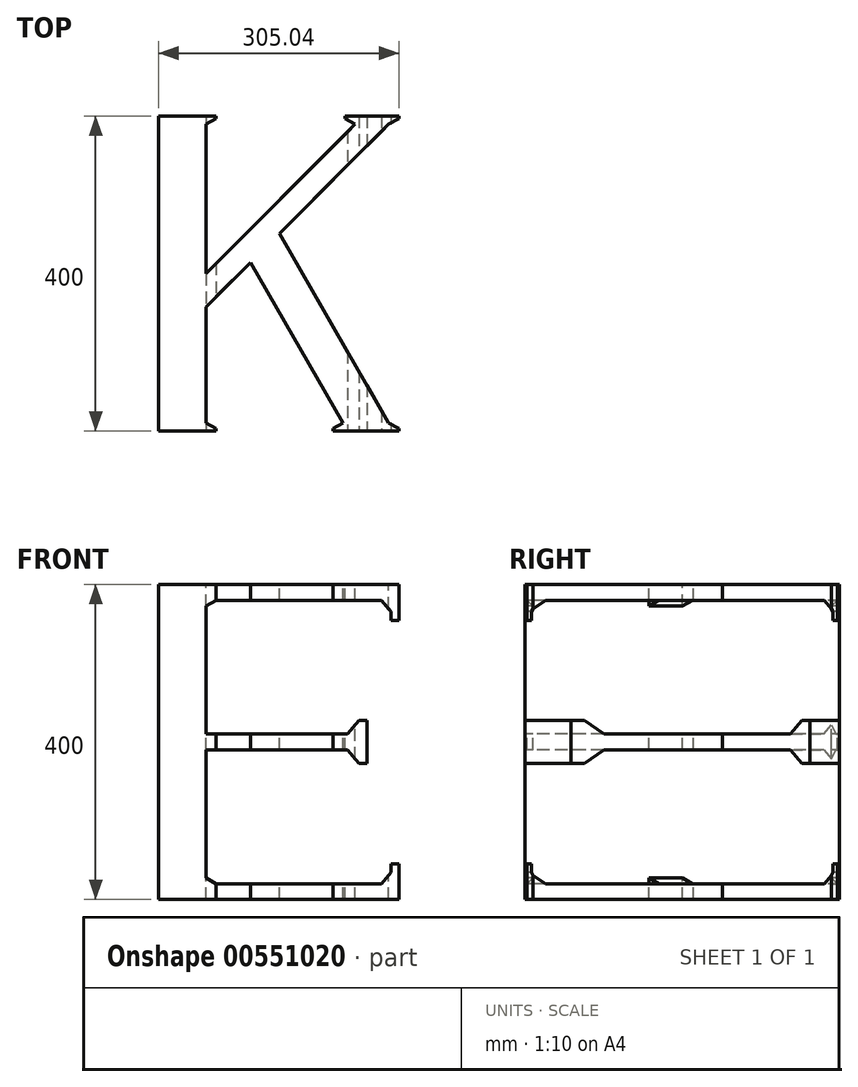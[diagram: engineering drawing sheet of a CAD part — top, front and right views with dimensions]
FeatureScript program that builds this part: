
annotation { "Feature Type Name" : "Feature", "Feature Type Description" : "" }
export const myFeature = defineFeature(function(context is Context, id is Id, definition is map)
    precondition{}
    {
        {
            var Q0;
            Q0=qCreatedBy(makeId("Front.planeOp"),FACE);
            var sketch = newSketch(context, id + "F0", { "sketchPlane" : qUnion([Q0])});
            skLineSegment(sketch, "E0.bottom", {"start": v(-197.15, 238.44) * mm, "end": v(107.89, 238.44) * mm});
            skLineSegment(sketch, "E0.top", {"start": v(-197.15, -161.56) * mm, "end": v(107.89, -161.56) * mm});
            skLineSegment(sketch, "E0.left", {"start": v(-197.15, 238.44) * mm, "end": v(-197.15, -161.56) * mm});
            skLineSegment(sketch, "E0.right", {"start": v(107.89, 238.44) * mm, "end": v(107.89, -161.56) * mm});
            skSolve(sketch);
        }
        {
            var Q0;
            Q0 = qSketchRegion(id + "F0", true);
            extrude(context, id + "F1", {"entities" : qUnion([Q0]), "depth" : 400 * mm, "offsetDistance" : 25.4 * mm});
        }
        {
            var Q0;
            Q0=makeQuery(id+"F1.opExtrude","SWEPT_FACE",FACE,{"disambiguationData":[OSD([sQuery(id+"F0.wireOp",EDGE,"E0.bottom")])]});
            var sketch = newSketch(context, id + "F2", { "sketchPlane" : qUnion([Q0])});
            skLineSegment(sketch, "E1", {"start": v(-197.15, -200) * mm, "end": v(0, -200) * mm, "construction": true});
            skLineSegment(sketch, "E2", {"start": v(-154.16, -400) * mm, "end": v(-154.16, -217.1) * mm, "construction": true});
            skLineSegment(sketch, "E3.MirrorCS", {"start": v(-137.15, -10.38) * mm, "end": v(-137.15, -200) * mm});
            skLineSegment(sketch, "E4.MirrorCS", {"start": v(-124.16, -2.88) * mm, "end": v(-137.15, -10.38) * mm});
            skLineSegment(sketch, "E5.MirrorCS", {"start": v(-124.16, -397.12) * mm, "end": v(-137.15, -389.62) * mm});
            skLineSegment(sketch, "E6", {"start": v(-124.16, -2.88) * mm, "end": v(-124.16, 0) * mm});
            skLineSegment(sketch, "E7", {"start": v(-124.16, -397.12) * mm, "end": v(-124.16, -400) * mm});
            skLineSegment(sketch, "E8", {"start": v(-137.15, -200) * mm, "end": v(52.47, -10.38) * mm});
            skLineSegment(sketch, "E9", {"start": v(-171.17, -10.38) * mm, "end": v(-197.15, -10.38) * mm, "construction": true});
            skLineSegment(sketch, "E10", {"start": v(52.47, -10.38) * mm, "end": v(39.48, -2.88) * mm});
            skLineSegment(sketch, "E11", {"start": v(39.48, -2.88) * mm, "end": v(39.48, 0) * mm});
            skLineSegment(sketch, "E12", {"start": v(-184.16, -10.38) * mm, "end": v(107.89, -10.38) * mm, "construction": true});
            skLineSegment(sketch, "E13", {"start": v(-137.15, -242.43) * mm, "end": v(-80.52, -185.8) * mm});
            skLineSegment(sketch, "E14", {"start": v(94.9, -10.38) * mm, "end": v(107.89, -2.88) * mm});
            skLineSegment(sketch, "E15", {"start": v(107.89, -2.88) * mm, "end": v(107.89, 0) * mm});
            skLineSegment(sketch, "E16", {"start": v(-80.52, -185.8) * mm, "end": v(37.16, -389.62) * mm});
            skLineSegment(sketch, "E17", {"start": v(-43.91, -149.2) * mm, "end": v(94.9, -389.62) * mm});
            skLineSegment(sketch, "E18", {"start": v(-171.17, -389.62) * mm, "end": v(107.89, -389.62) * mm, "construction": true});
            skLineSegment(sketch, "E19", {"start": v(94.9, -10.38) * mm, "end": v(94.9, -400) * mm, "construction": true});
            skPoint(sketch, "E20", {"position": v(94.9, -389.62) * mm});
            skLineSegment(sketch, "E21.MirrorCS", {"start": v(107.89, -397.12) * mm, "end": v(94.9, -389.62) * mm});
            skLineSegment(sketch, "E22.MirrorCS", {"start": v(37.16, -389.62) * mm, "end": v(24.17, -397.12) * mm});
            skLineSegment(sketch, "E23", {"start": v(24.17, -397.12) * mm, "end": v(24.17, -400) * mm});
            skLineSegment(sketch, "E24", {"start": v(107.89, -397.12) * mm, "end": v(107.89, -400) * mm});
            skPoint(sketch, "E25.orphan", {"position": v(39.33, -393.37) * mm});
            skPoint(sketch, "E26.orphan", {"position": v(97.06, -393.37) * mm});
            skLineSegment(sketch, "E27.trimOffspring", {"start": v(-43.91, -149.2) * mm, "end": v(94.9, -10.38) * mm});
            skLineSegment(sketch, "E28.trimOffspring", {"start": v(-137.15, -242.43) * mm, "end": v(-137.15, -389.62) * mm});
            skSolve(sketch);
        }
        {
            var Q0;
            Q0=makeQuery(id+"F1.opExtrude","CAP_FACE",FACE,{"disambiguationData":[OSD([sQuery(id+"F0.wireOp",EDGE,"E0.bottom"),sQuery(id+"F0.wireOp",EDGE,"E0.top"),sQuery(id+"F0.wireOp",EDGE,"E0.left"),sQuery(id+"F0.wireOp",EDGE,"E0.right")])],"isStart":false});
            var sketch = newSketch(context, id + "F3", { "sketchPlane" : qUnion([Q0])});
            skLineSegment(sketch, "E29", {"start": v(-137.15, 210.94) * mm, "end": v(-124.16, 218.44) * mm});
            skLineSegment(sketch, "E30", {"start": v(-137.15, 210.94) * mm, "end": v(-137.15, -134.06) * mm});
            skLineSegment(sketch, "E31", {"start": v(-137.15, -134.06) * mm, "end": v(-124.16, -141.56) * mm});
            skLineSegment(sketch, "E32", {"start": v(-124.16, -141.56) * mm, "end": v(85.84, -141.56) * mm});
            skLineSegment(sketch, "E33", {"start": v(-137.15, 48.44) * mm, "end": v(42.85, 48.44) * mm});
            skLineSegment(sketch, "E34", {"start": v(42.85, 48.44) * mm, "end": v(57.2, 65.55) * mm});
            skLineSegment(sketch, "E35", {"start": v(57.2, 65.55) * mm, "end": v(67.2, 65.55) * mm});
            skLineSegment(sketch, "E36", {"start": v(67.2, 65.55) * mm, "end": v(67.2, 11.33) * mm});
            skLineSegment(sketch, "E37", {"start": v(-197.15, 210.94) * mm, "end": v(-96.96, 210.94) * mm, "construction": true});
            skLineSegment(sketch, "E38", {"start": v(-197.15, 38.44) * mm, "end": v(107.89, 38.44) * mm, "construction": true});
            skLineSegment(sketch, "E39", {"start": v(85.84, -141.56) * mm, "end": v(97.89, -127.2) * mm});
            skLineSegment(sketch, "E40", {"start": v(97.89, -116.2) * mm, "end": v(97.89, -127.2) * mm});
            skLineSegment(sketch, "E41.MirrorCS", {"start": v(-137.15, 28.44) * mm, "end": v(42.85, 28.44) * mm});
            skLineSegment(sketch, "E42.MirrorCS", {"start": v(42.85, 28.44) * mm, "end": v(57.2, 11.33) * mm});
            skLineSegment(sketch, "E43.MirrorCS", {"start": v(57.2, 11.33) * mm, "end": v(67.2, 11.33) * mm});
            skLineSegment(sketch, "E44.MirrorCS", {"start": v(85.84, 218.44) * mm, "end": v(97.89, 204.08) * mm});
            skLineSegment(sketch, "E45.MirrorCS", {"start": v(97.89, 193.08) * mm, "end": v(97.89, 204.08) * mm});
            skLineSegment(sketch, "E46.MirrorCS", {"start": v(107.89, 193.08) * mm, "end": v(97.89, 193.08) * mm});
            skLineSegment(sketch, "E47.MirrorCS", {"start": v(-124.16, 218.44) * mm, "end": v(85.84, 218.44) * mm});
            skLineSegment(sketch, "E48", {"start": v(97.89, -116.2) * mm, "end": v(107.89, -116.2) * mm});
            skSolve(sketch);
        }
        {
            var Q0;
            Q0=makeQuery(id+"F1.opExtrude","SWEPT_FACE",FACE,{"disambiguationData":[OSD([sQuery(id+"F0.wireOp",EDGE,"E0.left")])]});
            var sketch = newSketch(context, id + "F4", { "sketchPlane" : qUnion([Q0])});
            skLineSegment(sketch, "E49.bottom", {"start": v(30, 208.44) * mm, "end": v(370, 208.44) * mm});
            skLineSegment(sketch, "E49.top", {"start": v(30, -131.56) * mm, "end": v(370, -131.56) * mm});
            skLineSegment(sketch, "E49.left", {"start": v(30, 208.44) * mm, "end": v(30, -131.56) * mm});
            skLineSegment(sketch, "E49.right", {"start": v(370, 208.44) * mm, "end": v(370, -131.56) * mm});
            skLineSegment(sketch, "E50", {"start": v(241.23, 208.44) * mm, "end": v(275.87, 188.44) * mm});
            skLineSegment(sketch, "E51", {"start": v(275.87, 188.44) * mm, "end": v(275.87, -23.46) * mm});
            skLineSegment(sketch, "E52", {"start": v(355.51, 208.44) * mm, "end": v(320.87, 188.44) * mm});
            skLineSegment(sketch, "E53", {"start": v(320.87, 188.44) * mm, "end": v(320.87, -23.46) * mm});
            skArc(sketch, "E54", {"start": v(118.53, -50.93) * mm, "mid": v(232.1, -128.53) * mm, "end": v(320.87, -23.46) * mm});
            skLineSegment(sketch, "E55", {"start": v(275.87, 188.44) * mm, "end": v(370, 188.44) * mm, "construction": true});
            skArc(sketch, "E56", {"start": v(137.57, -63.08) * mm, "mid": v(221.66, -95.39) * mm, "end": v(275.87, -23.46) * mm});
            skPoint(sketch, "E57", {"position": v(139.78, -38.63) * mm});
            skArc(sketch, "E58", {"start": v(137.57, -63.08) * mm, "mid": v(152.99, -17.94) * mm, "end": v(118.53, -50.93) * mm});
            skPoint(sketch, "E59.orphan", {"position": v(131.44, -50.93) * mm});
            skSolve(sketch);
        }
        {
            var Q0;
            Q0=makeQuery(id+"F2.imprint","IMPRINT",FACE,{"disambiguationData":[TD([[makeQuery(id+"F2.imprint","IMPRINT",EDGE,{"derivedFrom":sQuery(id+"F2.wireOp",EDGE,"E3.MirrorCS")}),1.0]])]});
            var Q1;
            {var subQ1=sQuery(id+"F2.wireOp",EDGE,"E14");Q1=makeQuery(id+"F2.imprint","IMPRINT",FACE,{"disambiguationData":[TD([[makeQuery(id+"F2.imprint","IMPRINT",EDGE,{"derivedFrom":subQ1}),-1.0]])]});}
            var Q2;
            Q2=makeQuery(id+"F2.imprint","IMPRINT",FACE,{"disambiguationData":[TD([[makeQuery(id+"F2.imprint","IMPRINT",EDGE,{"derivedFrom":sQuery(id+"F2.wireOp",EDGE,"E5.MirrorCS")}),-1.0]])]});
            extrude(context, id + "F5", {"entities" : qUnion([Q0, Q1, Q2]), "operationType" : NewBodyOperationType.REMOVE, "oppositeDirection" : true, "depth" : 481 * mm, "offsetDistance" : 25 * mm});
        }
        {
            var Q0;
            {var subQ1=sQuery(id+"F3.wireOp",EDGE,"E29");Q0=makeQuery(id+"F3.imprint","IMPRINT",FACE,{"disambiguationData":[TD([[makeQuery(id+"F3.imprint","IMPRINT",EDGE,{"derivedFrom":subQ1}),-1.0]])]});}
            var Q1;
            Q1 = qSketchRegion(id + "F2", true);
            extrude(context, id + "F6", {"entities" : qUnion([Q0, Q1]), "operationType" : NewBodyOperationType.REMOVE, "oppositeDirection" : true, "depth" : 640 * mm, "offsetDistance" : 25 * mm});
        }
    });
